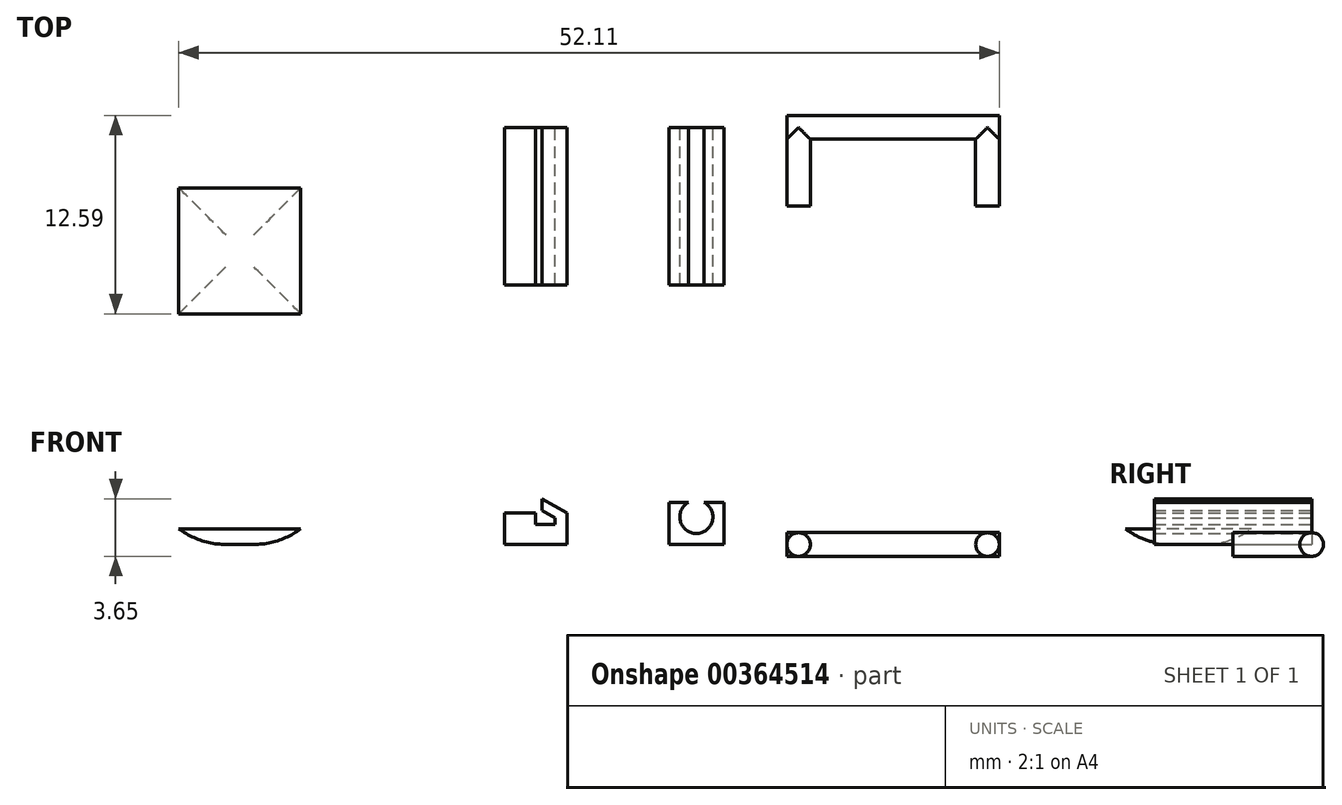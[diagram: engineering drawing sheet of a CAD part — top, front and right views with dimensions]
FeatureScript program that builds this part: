
annotation { "Feature Type Name" : "Feature", "Feature Type Description" : "" }
export const myFeature = defineFeature(function(context is Context, id is Id, definition is map)
    precondition{}
    {
        {
            var Q0;
            Q0=qCreatedBy(makeId("Front.planeOp"),FACE);
            var sketch = newSketch(context, id + "F0", { "sketchPlane" : qUnion([Q0])});
            skLineSegment(sketch, "E0.bottom", {"start": v(-23.51, 2) * mm, "end": v(1.49, 2) * mm});
            skLineSegment(sketch, "E0.top", {"start": v(-23.51, 0) * mm, "end": v(1.49, 0) * mm});
            skLineSegment(sketch, "E0.left", {"start": v(-23.51, 2) * mm, "end": v(-23.51, 0) * mm});
            skLineSegment(sketch, "E0.right", {"start": v(1.49, 2) * mm, "end": v(1.49, 0) * mm});
            skLineSegment(sketch, "E1.bottom", {"start": v(1.49, 2) * mm, "end": v(3.46, 2) * mm});
            skLineSegment(sketch, "E1.top", {"start": v(1.49, 0) * mm, "end": v(5.46, 0) * mm});
            skLineSegment(sketch, "E1.right", {"start": v(5.46, 2) * mm, "end": v(5.46, 0) * mm});
            skLineSegment(sketch, "E2", {"start": v(5.46, 2) * mm, "end": v(3.89, 2.9) * mm});
            skLineSegment(sketch, "E3", {"start": v(3.89, 2.15) * mm, "end": v(4.16, 2) * mm});
            skLineSegment(sketch, "E4", {"start": v(3.89, 2.15) * mm, "end": v(3.89, 2.9) * mm});
            skLineSegment(sketch, "E5", {"start": v(4.7, 1.68) * mm, "end": v(4.7, 1.28) * mm});
            skLineSegment(sketch, "E6", {"start": v(4.16, 2) * mm, "end": v(4.7, 1.68) * mm});
            skPoint(sketch, "E7.orphan", {"position": v(4.7, 0) * mm});
            skPoint(sketch, "E8", {"position": v(3.89, 1.28) * mm});
            skLineSegment(sketch, "E9", {"start": v(3.89, 1.28) * mm, "end": v(4.7, 1.28) * mm});
            skLineSegment(sketch, "E10", {"start": v(3.89, 1.28) * mm, "end": v(3.46, 1.28) * mm});
            skLineSegment(sketch, "E11", {"start": v(3.46, 1.28) * mm, "end": v(3.46, 2) * mm});
            skSolve(sketch);
        }
        {
            var Q0;
            Q0=makeQuery(id+"F0.imprint","IMPRINT",FACE,{"disambiguationData":[TD([[makeQuery(id+"F0.imprint","IMPRINT",EDGE,{"derivedFrom":sQuery(id+"F0.wireOp",EDGE,"E1.top")}),1.0]])]});
            var Q1;
            {var subQ0=sQuery(id+"F0.wireOp",EDGE,"E2");Q1=makeQuery(id+"F0.imprint","IMPRINT",FACE,{"disambiguationData":[TD([[makeQuery(id+"F0.imprint","IMPRINT",EDGE,{"derivedFrom":subQ0}),1.0]])]});}
            extrude(context, id + "F1", {"entities" : qUnion([Q0, Q1]), "depth" : 10 * mm});
        }
        {
            var Q0;
            Q0=qCreatedBy(makeId("Top.planeOp"),FACE);
            var sketch = newSketch(context, id + "F2", { "sketchPlane" : qUnion([Q0])});
            skLineSegment(sketch, "E12.bottom", {"start": v(-19.2, -3.84) * mm, "end": v(-11.44, -3.84) * mm});
            skLineSegment(sketch, "E12.top", {"start": v(-19.2, -11.84) * mm, "end": v(-11.44, -11.84) * mm});
            skLineSegment(sketch, "E12.left", {"start": v(-19.2, -3.84) * mm, "end": v(-19.2, -11.84) * mm});
            skLineSegment(sketch, "E12.right", {"start": v(-11.44, -3.84) * mm, "end": v(-11.44, -11.84) * mm});
            skSolve(sketch);
        }
        {
            var Q0;
            Q0=makeQuery(id+"F2.imprint","IMPRINT",FACE,{"disambiguationData":[TD([[makeQuery(id+"F2.imprint","IMPRINT",EDGE,{"derivedFrom":sQuery(id+"F2.wireOp",EDGE,"E12.bottom")}),-1.0]])]});
            extrude(context, id + "F3", {"entities" : qUnion([Q0]), "depth" : 1 * mm});
        }
        {
            var Q0;
            Q0=makeQuery(id+"F3.opExtrude","CAP_FACE",FACE,{"disambiguationData":[OSD([sQuery(id+"F2.wireOp",EDGE,"E12.bottom"),sQuery(id+"F2.wireOp",EDGE,"E12.top"),sQuery(id+"F2.wireOp",EDGE,"E12.left"),sQuery(id+"F2.wireOp",EDGE,"E12.right")])],"isStart":true});
            fillet(context, id + "F4", {"entities" : qUnion([Q0]), "radius" : 5 * mm, "tangentPropagation" : true, "allowEdgeOverflow" : false});
        }
        {
            var Q0;
            Q0=qCreatedBy(makeId("Front.planeOp"),FACE);
            var sketch = newSketch(context, id + "F5", { "sketchPlane" : qUnion([Q0])});
            skLineSegment(sketch, "E13.bottom", {"start": v(11.93, 3.5) * mm, "end": v(15.43, 3.5) * mm});
            skLineSegment(sketch, "E13.top", {"start": v(11.93, 0) * mm, "end": v(15.43, 0) * mm});
            skLineSegment(sketch, "E13.left", {"start": v(11.93, 3.5) * mm, "end": v(11.93, 0) * mm});
            skLineSegment(sketch, "E13.right", {"start": v(15.43, 3.5) * mm, "end": v(15.43, 0) * mm});
            skCircle(sketch, "E14", {"center": v(13.68, 1.75) * mm, "radius": 1.05 * mm});
            skPoint(sketch, "E14.centerSnap0", {"position": v(11.93, 1.75) * mm});
            skPoint(sketch, "E15", {"position": v(13.68, 3.5) * mm});
            skLineSegment(sketch, "E16", {"start": v(11.93, 2.67) * mm, "end": v(15.43, 2.67) * mm});
            skPoint(sketch, "E17", {"position": v(13.18, 2.67) * mm});
            skPoint(sketch, "E18", {"position": v(14.18, 2.67) * mm});
            skSolve(sketch);
        }
        {
            var Q0;
            {var subQ5=sQuery(id+"F5.wireOp",EDGE,"E13.top");Q0=makeQuery(id+"F5.imprint","IMPRINT",FACE,{"disambiguationData":[TD([[makeQuery(id+"F5.imprint","IMPRINT",EDGE,{"derivedFrom":subQ5}),1.0]])]});}
            extrude(context, id + "F6", {"entities" : qUnion([Q0]), "depth" : 10 * mm});
        }
        {
            var Q0;
            Q0=qCreatedBy(makeId("Front.planeOp"),FACE);
            var sketch = newSketch(context, id + "F7", { "sketchPlane" : qUnion([Q0])});
            skCircle(sketch, "E19", {"center": v(32.17, 0) * mm, "radius": 0.75 * mm});
            skCircle(sketch, "E20", {"center": v(20.17, 0) * mm, "radius": 0.75 * mm});
            skPoint(sketch, "E21", {"position": v(20.92, 0) * mm});
            skPoint(sketch, "E22", {"position": v(31.42, 0) * mm});
            skPoint(sketch, "E23", {"position": v(32.92, 0) * mm});
            skPoint(sketch, "E24", {"position": v(19.42, 0) * mm});
            skLineSegment(sketch, "E25.bottom", {"start": v(32.92, 0) * mm, "end": v(19.42, 0) * mm});
            skLineSegment(sketch, "E25.top", {"start": v(32.92, -0.75) * mm, "end": v(19.42, -0.75) * mm});
            skLineSegment(sketch, "E25.left", {"start": v(32.92, 0) * mm, "end": v(32.92, -0.75) * mm});
            skLineSegment(sketch, "E25.right", {"start": v(19.42, 0) * mm, "end": v(19.42, -0.75) * mm});
            skSolve(sketch);
        }
        {
            var Q0;
            Q0=makeQuery(id+"F7.imprint","IMPRINT",FACE,{"disambiguationData":[TD([[makeQuery(id+"F7.imprint","IMPRINT",EDGE,{"derivedFrom":sQuery(id+"F7.wireOp",EDGE,"E20")}),1.0]])]});
            var Q1;
            Q1=makeQuery(id+"F7.imprint","IMPRINT",FACE,{"disambiguationData":[TD([[makeQuery(id+"F7.imprint","IMPRINT",EDGE,{"derivedFrom":sQuery(id+"F7.wireOp",EDGE,"E19")}),1.0]])]});
            var Q2;
            {var subQ0=sQuery(id+"F7.wireOp",EDGE,"E25.bottom");var subQ1=sQuery(id+"F7.wireOp",EDGE,"E19");var subQ3=makeQuery(id+"F7.imprint","INTERSECT",VERTEX,{"derivedFrom":[subQ1,subQ0]});Q2=makeQuery(id+"F7.imprint","IMPRINT",FACE,{"disambiguationData":[TD([[makeQuery(id+"F7.imprint","IMPRINT",EDGE,{"disambiguationData":[TD([[subQ3,1.0]])],"derivedFrom":subQ1}),1.0]])]});}
            var Q3;
            {var subQ0=sQuery(id+"F7.wireOp",EDGE,"E25.bottom");var subQ1=sQuery(id+"F7.wireOp",EDGE,"E20");var subQ3=makeQuery(id+"F7.imprint","INTERSECT",VERTEX,{"derivedFrom":[subQ1,subQ0]});Q3=makeQuery(id+"F7.imprint","IMPRINT",FACE,{"disambiguationData":[TD([[makeQuery(id+"F7.imprint","IMPRINT",EDGE,{"disambiguationData":[TD([[subQ3,-1.0]])],"derivedFrom":subQ1}),1.0]])]});}
            extrude(context, id + "F8", {"entities" : qUnion([Q0, Q1, Q2, Q3]), "depth" : 5 * mm});
        }
        {
            var Q0;
            {var subQ0=sQuery(id+"F7.wireOp",EDGE,"E25.left");Q0=makeQuery(id+"F7.imprint","IMPRINT",FACE,{"disambiguationData":[TD([[makeQuery(id+"F7.imprint","IMPRINT",EDGE,{"derivedFrom":subQ0}),-1.0]])]});}
            var Q1;
            {var subQ0=sQuery(id+"F7.wireOp",EDGE,"E25.bottom");var subQ1=sQuery(id+"F7.wireOp",EDGE,"E19");var subQ2=makeQuery(id+"F7.imprint","INTERSECT",VERTEX,{"derivedFrom":[subQ1,subQ0]});Q1=makeQuery(id+"F7.imprint","IMPRINT",FACE,{"disambiguationData":[TD([[makeQuery(id+"F7.imprint","IMPRINT",EDGE,{"disambiguationData":[TD([[subQ2,-1.0]])],"derivedFrom":subQ1}),1.0]])]});}
            var Q2;
            {var subQ0=sQuery(id+"F7.wireOp",EDGE,"E25.bottom");var subQ1=sQuery(id+"F7.wireOp",EDGE,"E19");var subQ2=makeQuery(id+"F7.imprint","INTERSECT",VERTEX,{"derivedFrom":[subQ1,subQ0]});Q2=makeQuery(id+"F7.imprint","IMPRINT",FACE,{"disambiguationData":[TD([[makeQuery(id+"F7.imprint","IMPRINT",EDGE,{"disambiguationData":[TD([[subQ2,-1.0]])],"derivedFrom":subQ1}),-1.0]])]});}
            var Q3;
            {var subQ1=sQuery(id+"F7.wireOp",EDGE,"E20");var subQ3=makeQuery(id+"F7.imprint","INTERSECT",VERTEX,{"derivedFrom":[subQ1,sQuery(id+"F7.wireOp",EDGE,"E25.top")]});Q3=makeQuery(id+"F7.imprint","IMPRINT",FACE,{"disambiguationData":[TD([[makeQuery(id+"F7.imprint","IMPRINT",EDGE,{"disambiguationData":[TD([[subQ3,-1.0]])],"derivedFrom":subQ1}),1.0]])]});}
            var Q4;
            {var subQ0=sQuery(id+"F7.wireOp",EDGE,"E25.right");Q4=makeQuery(id+"F7.imprint","IMPRINT",FACE,{"disambiguationData":[TD([[makeQuery(id+"F7.imprint","IMPRINT",EDGE,{"derivedFrom":subQ0}),1.0]])]});}
            var Q5;
            Q5=sQuery(id+"F7.wireOp",EDGE,"E25.bottom");
            revolve(context, id + "F9", {"operationType" : NewBodyOperationType.ADD, "entities" : qUnion([Q0, Q1, Q2, Q3, Q4]), "axis" : qUnion([Q5]), "revolveType" : RevolveType.FULL});
        }
        {
            var Q0;
            Q0=makeQuery(id+"F8.opExtrude","CAP_FACE",FACE,{"disambiguationData":[OSD([sQuery(id+"F7.wireOp",EDGE,"E19")])],"isStart":false});
            var sketch = newSketch(context, id + "F10", { "sketchPlane" : qUnion([Q0])});
            skPoint(sketch, "E26", {"position": v(26.17, 0) * mm});
            skSolve(sketch);
        }
    });
